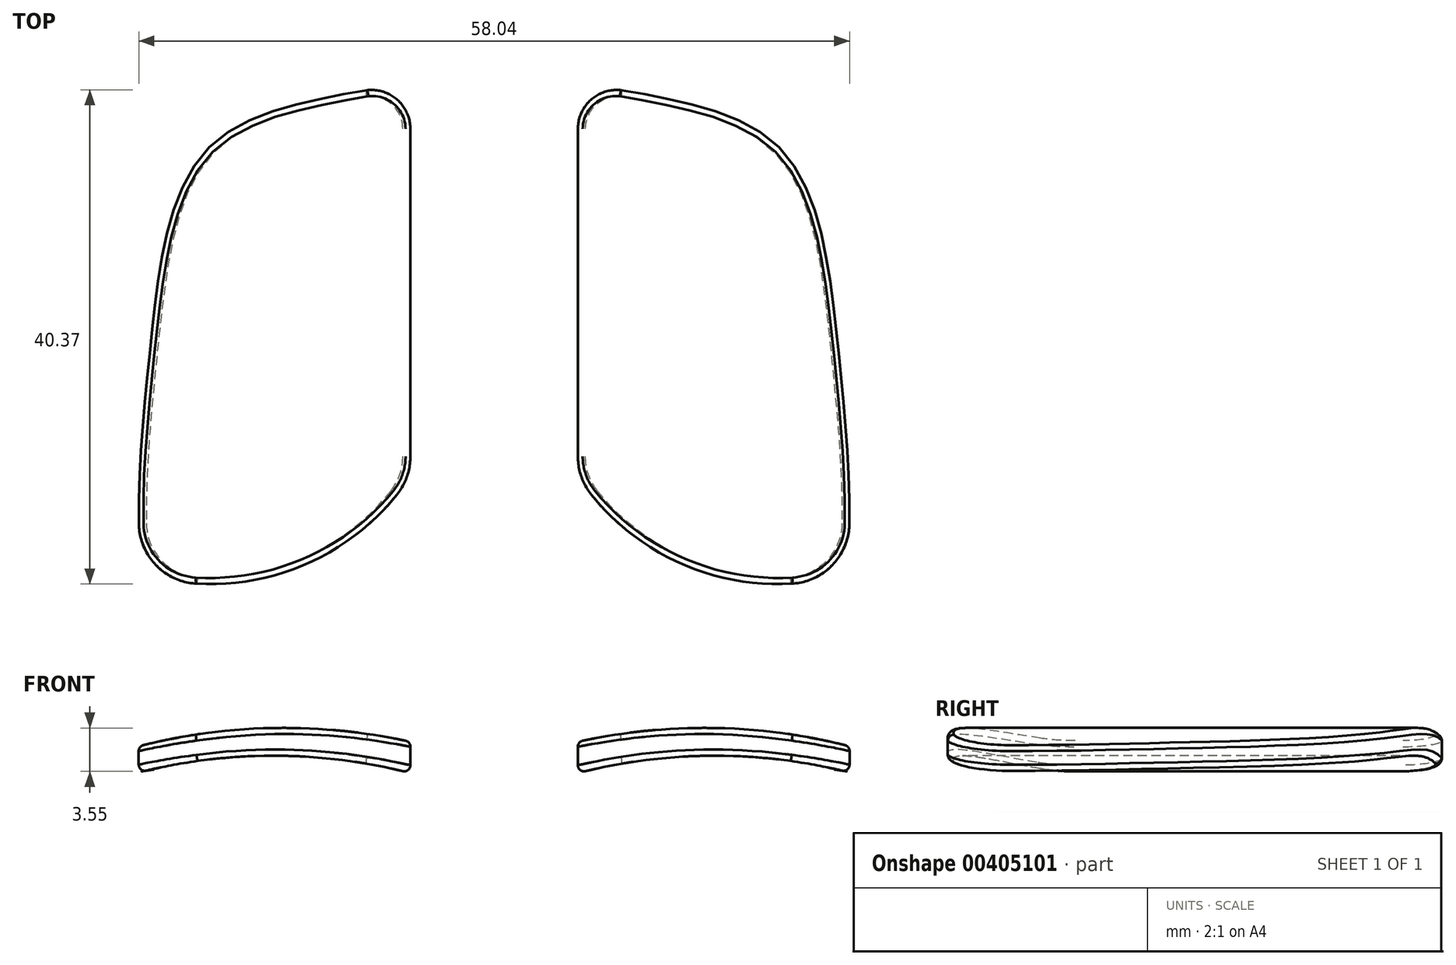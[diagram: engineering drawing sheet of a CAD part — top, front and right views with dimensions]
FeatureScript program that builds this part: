
annotation { "Feature Type Name" : "Feature", "Feature Type Description" : "" }
export const myFeature = defineFeature(function(context is Context, id is Id, definition is map)
    precondition{}
    {
        {
            var Q0;
            Q0=qCreatedBy(makeId("Top.planeOp"),FACE);
            var sketch = newSketch(context, id + "F0", { "sketchPlane" : qUnion([Q0])});
            skLineSegment(sketch, "E0", {"start": v(0, 22.3) * mm, "end": v(-6.84, 15) * mm});
            skLineSegment(sketch, "E1", {"start": v(-6.84, 15) * mm, "end": v(-6.84, -15) * mm});
            skLineSegment(sketch, "E2", {"start": v(-6.84, -15) * mm, "end": v(0, -22.3) * mm});
            skLineSegment(sketch, "E3", {"start": v(0, -22.3) * mm, "end": v(7, -12.54) * mm});
            skArc(sketch, "E4", {"start": v(7, -12.54) * mm, "mid": v(10.14, -1.9) * mm, "end": v(6.01, 8.38) * mm});
            skLineSegment(sketch, "E5", {"start": v(6.01, 8.38) * mm, "end": v(0, 15.3) * mm});
            skLineSegment(sketch, "E6", {"start": v(0, 15.3) * mm, "end": v(0, 22.3) * mm});
            skLineSegment(sketch, "E7", {"start": v(10.16, 10.65) * mm, "end": v(10.16, -7.16) * mm, "construction": true});
            skLineSegment(sketch, "E8", {"start": v(-6.84, 0) * mm, "end": v(0, 0) * mm, "construction": true});
            skSolve(sketch);
        }
        {
            var Q0;
            Q0=qCreatedBy(makeId("Top.planeOp"),FACE);
            var sketch = newSketch(context, id + "F1", { "sketchPlane" : qUnion([Q0])});
            skLineSegment(sketch, "E9.0", {"start": v(-6.84, 15) * mm, "end": v(-6.84, -15) * mm, "construction": true});
            skLineSegment(sketch, "E10", {"start": v(-5.86, 13.88) * mm, "end": v(-5.86, -14.5) * mm});
            skArc(sketch, "E11", {"start": v(-5.86, -14.5) * mm, "mid": v(3.8, -22.13) * mm, "end": v(16.1, -22.48) * mm});
            skFitSpline(sketch, "E12", {"points": [v(16.1, -22.48) * mm, v(14.65, -4.07) * mm, v(9.15, 3.15) * mm, v(2.43, 7.92) * mm, v(0, 15.57) * mm], "startDerivative": vector(1.29, 67.52) * mm, "endDerivative": vector(-12.79, 20.42) * mm, "construction": true});
            skArc(sketch, "E13", {"start": v(0, 15.57) * mm, "mid": v(-3.56, 16.93) * mm, "end": v(-5.86, 13.88) * mm, "construction": true});
            skFitSpline(sketch, "E14", {"points": [v(16.1, -22.48) * mm, v(15.36, -3.88) * mm, v(10.72, 12.2) * mm, v(1.3, 16.35) * mm, v(-2.3, 17.03) * mm], "startDerivative": vector(5.45, 57.26) * mm, "endDerivative": vector(-23.79, 2.92) * mm});
            skArc(sketch, "E15", {"start": v(-2.3, 17.03) * mm, "mid": v(-4.8, 16.26) * mm, "end": v(-5.86, 13.88) * mm});
            skSolve(sketch);
        }
        {
            var Q0;
            Q0 = qSketchRegion(id + "F1", true);
            extrude(context, id + "F2", {"entities" : qUnion([Q0]), "depth" : 5 * mm, "offsetDistance" : 25.4 * mm});
        }
        {
            var Q0;
            Q0=qCreatedBy(makeId("Front.planeOp"),FACE);
            var sketch = newSketch(context, id + "F3", { "sketchPlane" : qUnion([Q0])});
            skArc(sketch, "E16", {"start": v(17.02, 2.13) * mm, "mid": v(5.42, 3.8) * mm, "end": v(-6.23, 2.6) * mm});
            skArc(sketch, "E17", {"start": v(16.98, 0) * mm, "mid": v(5.32, 1.54) * mm, "end": v(-6.33, 0) * mm});
            skLineSegment(sketch, "E18", {"start": v(-6.23, 2.6) * mm, "end": v(-8.3, 5.64) * mm});
            skLineSegment(sketch, "E19", {"start": v(-8.3, 5.64) * mm, "end": v(-6.23, 7.36) * mm});
            skLineSegment(sketch, "E20", {"start": v(-6.23, 7.36) * mm, "end": v(18.16, 6.84) * mm});
            skLineSegment(sketch, "E21", {"start": v(18.16, 6.84) * mm, "end": v(19.27, 2.6) * mm});
            skLineSegment(sketch, "E22", {"start": v(19.27, 2.6) * mm, "end": v(17.02, 2.13) * mm});
            skLineSegment(sketch, "E23", {"start": v(16.98, 0) * mm, "end": v(18.51, -4.58) * mm});
            skLineSegment(sketch, "E24", {"start": v(18.51, -4.58) * mm, "end": v(-6.23, -4.58) * mm});
            skLineSegment(sketch, "E25", {"start": v(-6.23, -4.58) * mm, "end": v(-8.57, -1.8) * mm});
            skLineSegment(sketch, "E26", {"start": v(-8.57, -1.8) * mm, "end": v(-6.33, 0) * mm});
            skSolve(sketch);
        }
        {
            var Q0;
            Q0 = qSketchRegion(id + "F3", true);
            extrude(context, id + "F4", {"entities" : qUnion([Q0]), "operationType" : NewBodyOperationType.REMOVE, "endBound" : BoundingType.THROUGH_ALL, "oppositeDirection" : true, "depth" : 25.4 * mm, "offsetDistance" : 25.4 * mm, "hasSecondDirection" : true, "secondDirectionBound" : SecondDirectionBoundingType.THROUGH_ALL, "secondDirectionOppositeDirection" : false, "secondDirectionDepth" : 25.4 * mm});
        }
        {
            var Q0;
            Q0=makeQuery(id+"F2.opExtrude","SWEPT_EDGE",EDGE,{"disambiguationData":[OSD([sQuery(id+"F1.wireOp",EDGE,"E11"),sQuery(id+"F1.wireOp",EDGE,"E12")])]});
            var Q1;
            Q1=makeQuery(id+"F2.opExtrude","SWEPT_EDGE",EDGE,{"disambiguationData":[OSD([sQuery(id+"F1.wireOp",EDGE,"E10"),sQuery(id+"F1.wireOp",EDGE,"E11")])]});
            fillet(context, id + "F5", {"entities" : qUnion([Q0, Q1]), "tangentPropagation" : true, "radius" : 5 * mm, "defaultsChanged" : false, "vertexSettings" : [], "allowEdgeOverflow" : false});
        }
        {
            var Q0;
            Q0=makeQuery(id+"F4.boolean.opBoolean","COPY",FACE,{"derivedFrom":makeQuery(id+"F4.opExtrude","SWEPT_FACE",FACE,{"disambiguationData":[OSD([sQuery(id+"F3.wireOp",EDGE,"E17")])]})});
            var Q1;
            Q1=makeQuery(id+"F4.boolean.opBoolean","COPY",FACE,{"derivedFrom":makeQuery(id+"F4.opExtrude","SWEPT_FACE",FACE,{"disambiguationData":[OSD([sQuery(id+"F3.wireOp",EDGE,"E16")])]})});
            fillet(context, id + "F6", {"entities" : qUnion([Q0, Q1]), "tangentPropagation" : true, "radius" : .5 * mm, "defaultsChanged" : true, "vertexSettings" : [], "allowEdgeOverflow" : false});
        }
        {
            var Q0;
            Q0=qCreatedBy(makeId("Right.planeOp"),FACE);
            cPlane(context, id + "F7", {"entities" : qUnion([Q0]), "cplaneType" : CPlaneType.OFFSET, "offset" : 12.7 * mm, "oppositeDirection" : true, "width" : 152.4 * mm, "height" : 152.4 * mm});
        }
        {
            var Q0;
            Q0=makeQuery(id+"F2.opExtrude","SWEPT_BODY",BODY,{"disambiguationData":[OSD([sQuery(id+"F1.wireOp",EDGE,"E10"),sQuery(id+"F1.wireOp",EDGE,"E11"),sQuery(id+"F1.wireOp",EDGE,"E14"),sQuery(id+"F1.wireOp",EDGE,"E15")])]});
            var Q1;
            Q1=qCreatedBy(id+"F7.planeOp",FACE);
            mirror(context, id + "F8", {"entities" : qUnion([Q0]), "mirrorPlane" : qUnion([Q1])});
        }
    });
